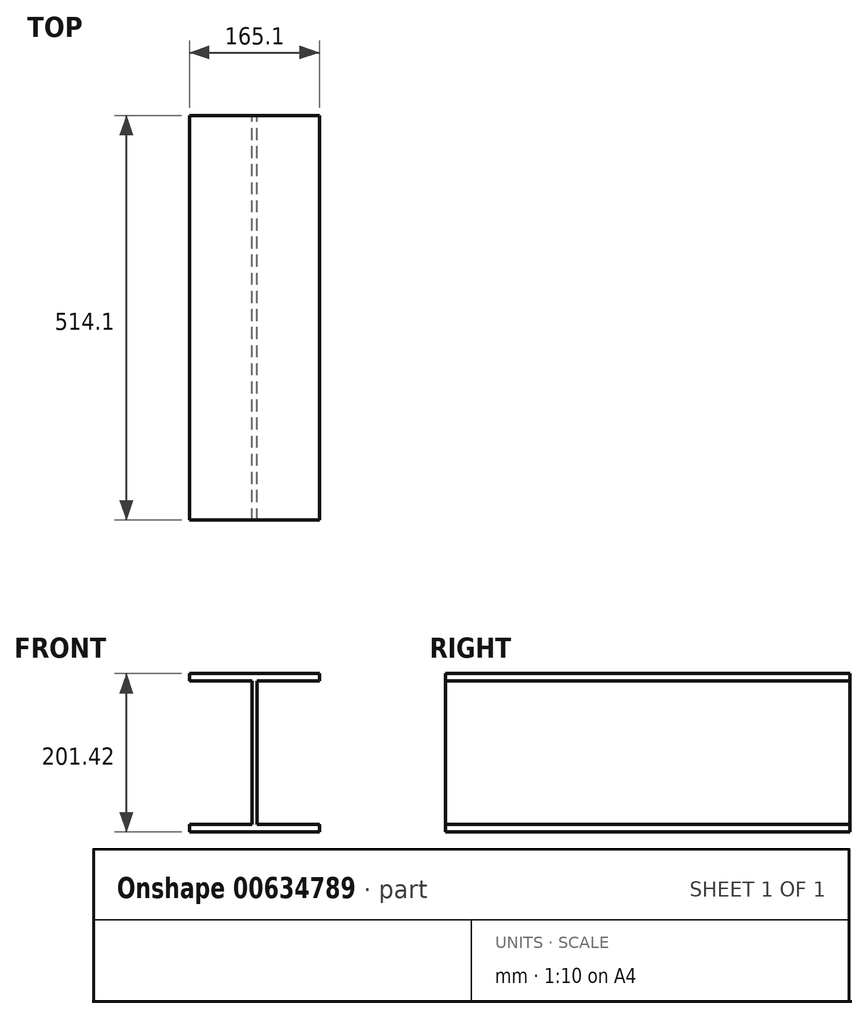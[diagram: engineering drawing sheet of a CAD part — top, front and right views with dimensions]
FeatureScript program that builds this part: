
annotation { "Feature Type Name" : "Feature", "Feature Type Description" : "" }
export const myFeature = defineFeature(function(context is Context, id is Id, definition is map)
    precondition{}
    {
        {
            var Q0;
            Q0=qCreatedBy(makeId("Front.planeOp"),FACE);
            var sketch = newSketch(context, id + "F0", { "sketchPlane" : qUnion([Q0])});
            skLineSegment(sketch, "E0", {"start": v(-82.55, 100.71) * mm, "end": v(82.55, 100.71) * mm});
            skLineSegment(sketch, "E1", {"start": v(82.55, 100.71) * mm, "end": v(82.55, 91.19) * mm});
            skLineSegment(sketch, "E2", {"start": v(82.55, 91.19) * mm, "end": v(3.17, 91.19) * mm});
            skLineSegment(sketch, "E3", {"start": v(3.17, 91.19) * mm, "end": v(3.18, -91.19) * mm});
            skLineSegment(sketch, "E4", {"start": v(3.18, -91.19) * mm, "end": v(82.55, -91.19) * mm});
            skLineSegment(sketch, "E5", {"start": v(-82.55, 100.71) * mm, "end": v(-82.55, 91.19) * mm});
            skLineSegment(sketch, "E6", {"start": v(-82.55, 91.19) * mm, "end": v(-3.18, 91.19) * mm});
            skLineSegment(sketch, "E7", {"start": v(-3.18, 91.19) * mm, "end": v(-3.17, -91.19) * mm});
            skLineSegment(sketch, "E8", {"start": v(-3.17, -91.19) * mm, "end": v(-82.55, -91.19) * mm});
            skLineSegment(sketch, "E9", {"start": v(-82.55, -91.19) * mm, "end": v(-82.55, -100.71) * mm});
            skLineSegment(sketch, "E10", {"start": v(-82.55, -100.71) * mm, "end": v(82.55, -100.71) * mm});
            skLineSegment(sketch, "E11", {"start": v(82.55, -100.71) * mm, "end": v(82.55, -91.19) * mm});
            skLineSegment(sketch, "E12", {"start": v(3.17, 91.19) * mm, "end": v(-3.17, -91.19) * mm, "construction": true});
            skSolve(sketch);
        }
        {
            var Q0;
            Q0=qSketchRegion(id+"F0",true);
            extrude(context, id + "F1", {"entities" : qUnion([Q0]), "depth" : 514.1 * mm, "offsetDistance" : 25.4 * mm});
        }
    });
